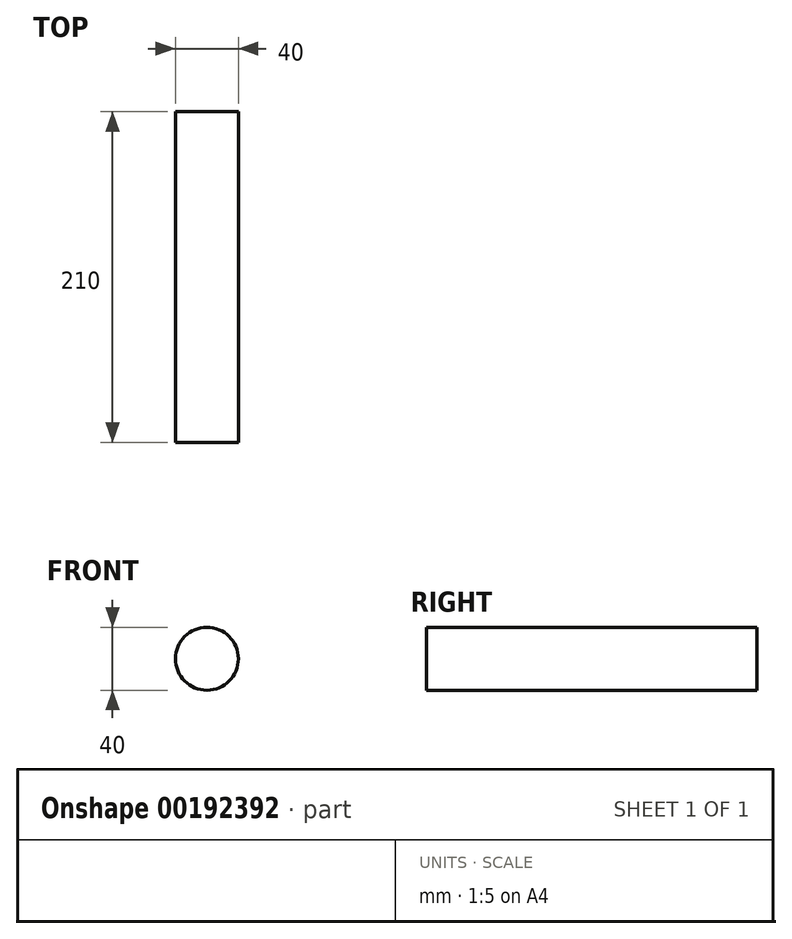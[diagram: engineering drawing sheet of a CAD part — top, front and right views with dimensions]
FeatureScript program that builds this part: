
annotation { "Feature Type Name" : "Feature", "Feature Type Description" : "" }
export const myFeature = defineFeature(function(context is Context, id is Id, definition is map)
    precondition{}
    {
        {
            var Q0;
            Q0=qCreatedBy(makeId("Front.planeOp"),FACE);
            var sketch = newSketch(context, id + "F0", { "sketchPlane" : qUnion([Q0])});
            skCircle(sketch, "E0", {"center": v(0, 0) * mm, "radius": 20 * mm});
            skSolve(sketch);
        }
        {
            var Q0;
            Q0 = qSketchRegion(id + "F0", true);
            extrude(context, id + "F1", {"entities" : qUnion([Q0]), "depth" : 210 * mm});
        }
    });
